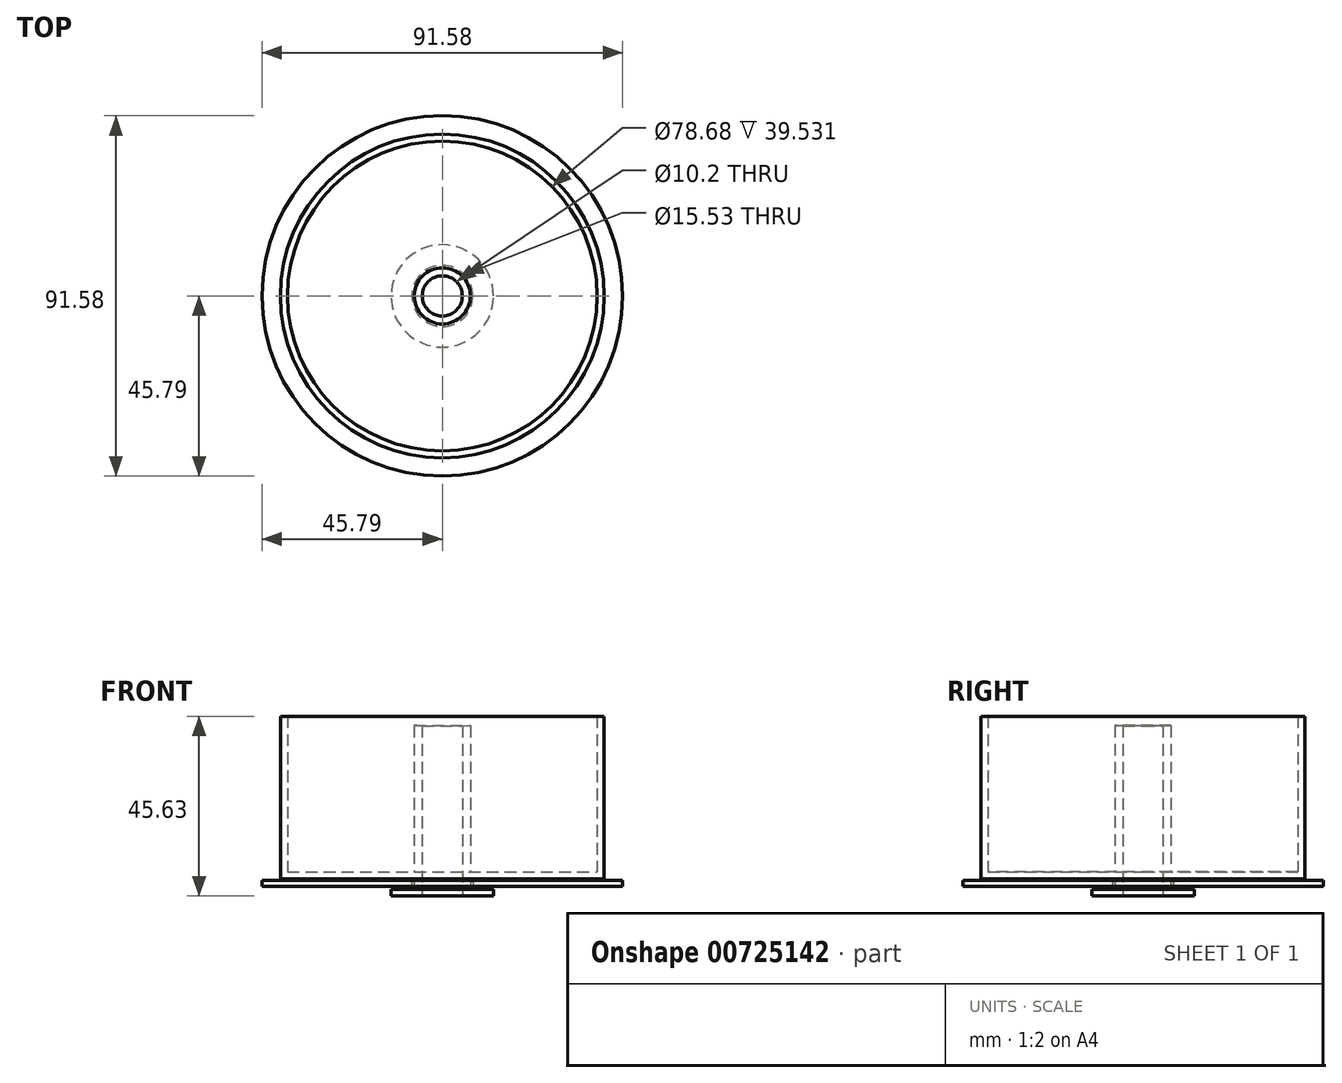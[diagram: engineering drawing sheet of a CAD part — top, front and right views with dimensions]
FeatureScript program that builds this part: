
annotation { "Feature Type Name" : "Feature", "Feature Type Description" : "" }
export const myFeature = defineFeature(function(context is Context, id is Id, definition is map)
    precondition{}
    {
        {
            var Q0;
            Q0=qCreatedBy(makeId("Front.planeOp"),FACE);
            var sketch = newSketch(context, id + "F0", { "sketchPlane" : qUnion([Q0])});
            skLineSegment(sketch, "E0", {"start": v(7.13, 0) * mm, "end": v(39.34, 0) * mm});
            skLineSegment(sketch, "E1", {"start": v(39.34, 0) * mm, "end": v(39.34, 39.53) * mm});
            skLineSegment(sketch, "E2.0", {"start": v(41.12, -1.78) * mm, "end": v(41.12, 39.53) * mm});
            skLineSegment(sketch, "E2.1", {"start": v(7.13, -1.78) * mm, "end": v(41.12, -1.78) * mm});
            skLineSegment(sketch, "E3", {"start": v(39.34, 39.53) * mm, "end": v(41.12, 39.53) * mm});
            skLineSegment(sketch, "E4", {"start": v(7.13, -1.78) * mm, "end": v(7.13, -4.49) * mm});
            skLineSegment(sketch, "E5", {"start": v(7.13, -4.49) * mm, "end": v(13, -4.49) * mm});
            skLineSegment(sketch, "E6", {"start": v(13, -4.49) * mm, "end": v(13, -6.1) * mm});
            skLineSegment(sketch, "E7", {"start": v(13, -6.1) * mm, "end": v(5.1, -6.1) * mm});
            skLineSegment(sketch, "E8", {"start": v(5.1, -6.1) * mm, "end": v(5.1, 0) * mm});
            skLineSegment(sketch, "E9.bottom", {"start": v(7.76, -2.18) * mm, "end": v(45.8, -2.18) * mm});
            skLineSegment(sketch, "E9.top", {"start": v(7.76, -3.76) * mm, "end": v(45.8, -3.76) * mm});
            skLineSegment(sketch, "E9.left", {"start": v(7.76, -2.18) * mm, "end": v(7.76, -3.76) * mm});
            skLineSegment(sketch, "E9.right", {"start": v(45.8, -2.18) * mm, "end": v(45.8, -3.76) * mm});
            skLineSegment(sketch, "E10", {"start": v(0, 0) * mm, "end": v(0, 34.8) * mm, "construction": true});
            skLineSegment(sketch, "E11", {"start": v(5.1, 0) * mm, "end": v(5.1, 37.09) * mm});
            skLineSegment(sketch, "E12", {"start": v(7.13, 0) * mm, "end": v(7.13, 37.15) * mm});
            skLineSegment(sketch, "E13", {"start": v(5.1, 37.09) * mm, "end": v(7.13, 37.15) * mm});
            skSolve(sketch);
        }
        {
            var Q0;
            Q0=makeQuery(id+"F0.imprint","IMPRINT",FACE,{"disambiguationData":[TD([[makeQuery(id+"F0.imprint","IMPRINT",EDGE,{"derivedFrom":sQuery(id+"F0.wireOp",EDGE,"E0")}),-1.0]])]});
            var Q1;
            Q1=makeQuery(id+"F0.imprint","IMPRINT",FACE,{"disambiguationData":[TD([[makeQuery(id+"F0.imprint","IMPRINT",EDGE,{"derivedFrom":sQuery(id+"F0.wireOp",EDGE,"E9.bottom")}),-1.0]])]});
            var Q2;
            Q2=sQuery(id+"F0.wireOp",EDGE,"E10");
            revolve(context, id + "F1", {"surfaceOperationType" : NewSurfaceOperationType.NEW, "entities" : qUnion([Q0, Q1]), "axis" : qUnion([Q2]), "revolveType" : RevolveType.FULL});
        }
    });
